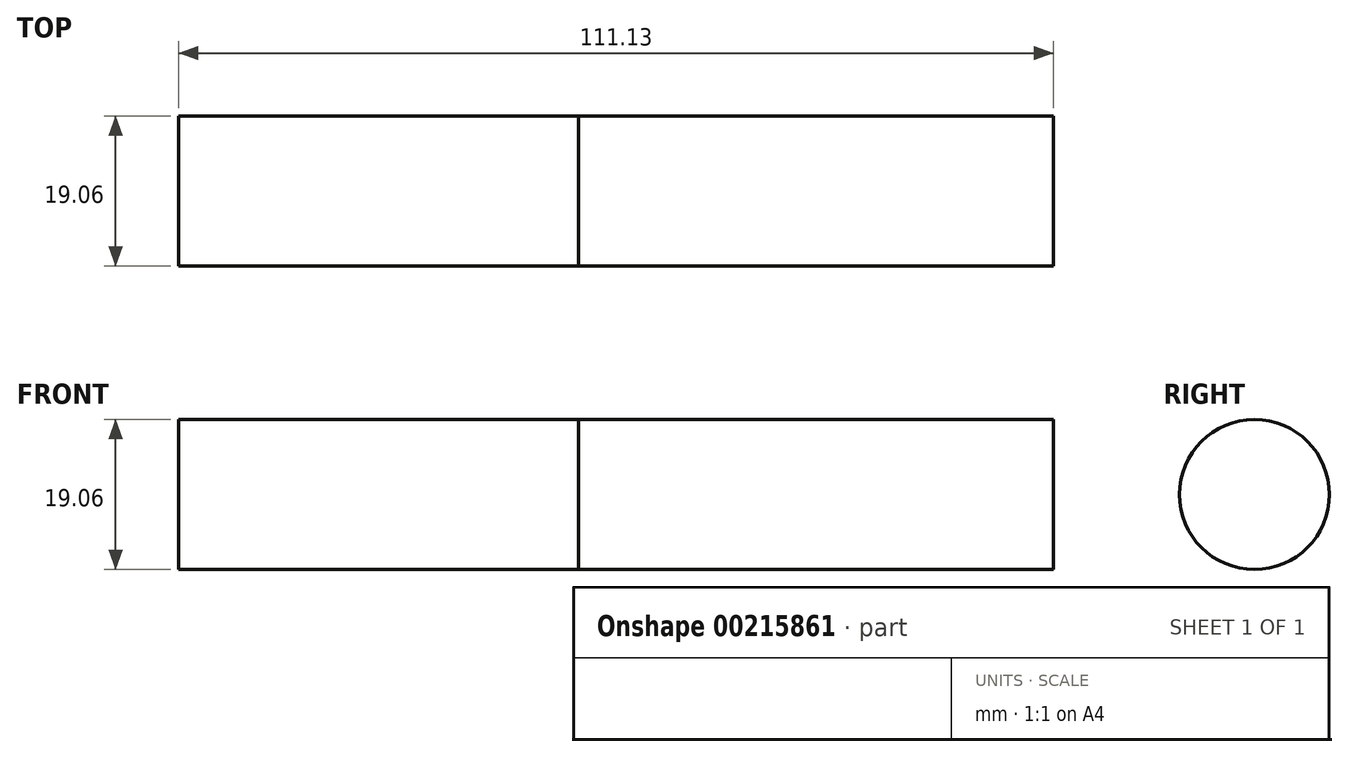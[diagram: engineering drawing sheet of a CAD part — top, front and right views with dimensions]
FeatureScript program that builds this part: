
annotation { "Feature Type Name" : "Feature", "Feature Type Description" : "" }
export const myFeature = defineFeature(function(context is Context, id is Id, definition is map)
    precondition{}
    {
        {
            var Q0;
            Q0=qCreatedBy(makeId("Right.planeOp"),FACE);
            var sketch = newSketch(context, id + "F0", { "sketchPlane" : qUnion([Q0])});
            skCircle(sketch, "E0", {"center": v(0, 0) * mm, "radius": 9.53 * mm});
            skSolve(sketch);
        }
        {
            var Q0;
            Q0=qSketchRegion(id+"F0",true);
            extrude(context, id + "F1", {"entities" : qUnion([Q0]), "depth" : 111.12 * mm});
        }
        {
            var Q0;
            Q0=qSketchRegion(id+"F0",true);
            extrude(context, id + "F2", {"entities" : qUnion([Q0]), "depth" : 50.8 * mm});
        }
    });
